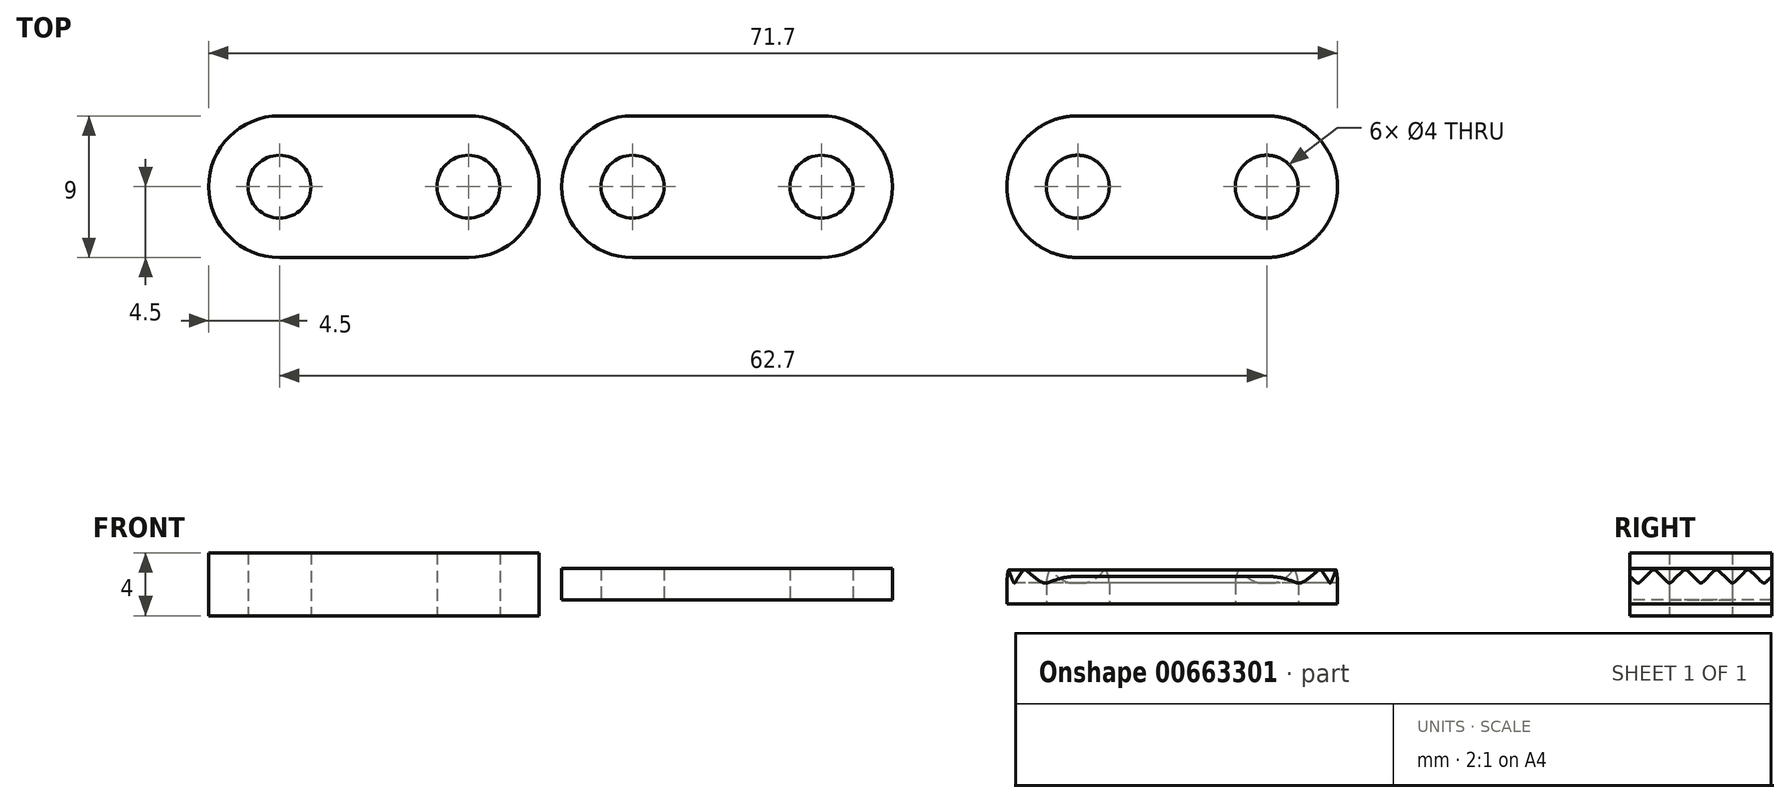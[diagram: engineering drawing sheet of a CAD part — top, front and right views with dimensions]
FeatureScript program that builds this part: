
annotation { "Feature Type Name" : "Feature", "Feature Type Description" : "" }
export const myFeature = defineFeature(function(context is Context, id is Id, definition is map)
    precondition{}
    {
        {
            var Q0;
            Q0=qCreatedBy(makeId("Top.planeOp"),FACE);
            var sketch = newSketch(context, id + "F0", { "sketchPlane" : qUnion([Q0])});
            skCircle(sketch, "E0", {"center": v(-56.7, 0) * mm, "radius": 4.5 * mm});
            skCircle(sketch, "E1", {"center": v(-44.7, 0) * mm, "radius": 4.5 * mm});
            skLineSegment(sketch, "E2", {"start": v(-44.7, 4.5) * mm, "end": v(-56.7, 4.5) * mm});
            skLineSegment(sketch, "E3", {"start": v(-56.7, -4.5) * mm, "end": v(-44.7, -4.5) * mm});
            skCircle(sketch, "E4", {"center": v(-56.7, 0) * mm, "radius": 2 * mm});
            skCircle(sketch, "E5", {"center": v(-44.7, 0) * mm, "radius": 2 * mm});
            skCircle(sketch, "E6", {"center": v(-34.28, 0) * mm, "radius": 4.5 * mm});
            skCircle(sketch, "E7", {"center": v(-22.28, 0) * mm, "radius": 4.5 * mm});
            skLineSegment(sketch, "E8", {"start": v(-22.28, 4.5) * mm, "end": v(-34.28, 4.5) * mm});
            skLineSegment(sketch, "E9", {"start": v(-34.28, -4.5) * mm, "end": v(-22.28, -4.5) * mm});
            skCircle(sketch, "E10", {"center": v(-34.28, 0) * mm, "radius": 2 * mm});
            skCircle(sketch, "E11", {"center": v(-22.28, 0) * mm, "radius": 2 * mm});
            skCircle(sketch, "E12", {"center": v(-6, 0) * mm, "radius": 4.5 * mm});
            skCircle(sketch, "E13", {"center": v(6, 0) * mm, "radius": 4.5 * mm});
            skLineSegment(sketch, "E14", {"start": v(6, 4.5) * mm, "end": v(-6, 4.5) * mm});
            skLineSegment(sketch, "E15", {"start": v(-6, -4.5) * mm, "end": v(6, -4.5) * mm});
            skCircle(sketch, "E16", {"center": v(-6, 0) * mm, "radius": 2 * mm});
            skCircle(sketch, "E17", {"center": v(6, 0) * mm, "radius": 2 * mm});
            skSolve(sketch);
        }
        {
            var Q0;
            Q0=makeQuery(id+"F0.imprint","IMPRINT",FACE,{"disambiguationData":[TD([[makeQuery(id+"F0.imprint","IMPRINT",EDGE,{"derivedFrom":sQuery(id+"F0.wireOp",EDGE,"E4")}),-1.0]])]});
            var Q1;
            Q1=makeQuery(id+"F0.imprint","IMPRINT",FACE,{"disambiguationData":[TD([[makeQuery(id+"F0.imprint","IMPRINT",EDGE,{"derivedFrom":sQuery(id+"F0.wireOp",EDGE,"E5")}),-1.0]])]});
            var Q2;
            {var subQ0=sQuery(id+"F0.wireOp",EDGE,"E2");Q2=makeQuery(id+"F0.imprint","IMPRINT",FACE,{"disambiguationData":[TD([[makeQuery(id+"F0.imprint","IMPRINT",EDGE,{"derivedFrom":subQ0}),1.0]])]});}
            extrude(context, id + "F1", {"entities" : qUnion([Q0, Q1, Q2]), "endBound" : BoundingType.SYMMETRIC, "depth" : 4 * mm, "offsetDistance" : 25 * mm});
        }
        {
            var Q0;
            Q0=makeQuery(id+"F0.imprint","IMPRINT",FACE,{"disambiguationData":[TD([[makeQuery(id+"F0.imprint","IMPRINT",EDGE,{"derivedFrom":sQuery(id+"F0.wireOp",EDGE,"E10")}),-1.0]])]});
            var Q1;
            {var subQ0=sQuery(id+"F0.wireOp",EDGE,"E8");Q1=makeQuery(id+"F0.imprint","IMPRINT",FACE,{"disambiguationData":[TD([[makeQuery(id+"F0.imprint","IMPRINT",EDGE,{"derivedFrom":subQ0}),1.0]])]});}
            var Q2;
            Q2=makeQuery(id+"F0.imprint","IMPRINT",FACE,{"disambiguationData":[TD([[makeQuery(id+"F0.imprint","IMPRINT",EDGE,{"derivedFrom":sQuery(id+"F0.wireOp",EDGE,"E11")}),-1.0]])]});
            extrude(context, id + "F2", {"entities" : qUnion([Q0, Q1, Q2]), "endBound" : BoundingType.SYMMETRIC, "depth" : 2 * mm, "offsetDistance" : 25 * mm});
        }
        {
            var Q0;
            Q0=makeQuery(id+"F0.imprint","IMPRINT",FACE,{"disambiguationData":[TD([[makeQuery(id+"F0.imprint","IMPRINT",EDGE,{"derivedFrom":sQuery(id+"F0.wireOp",EDGE,"E16")}),-1.0]])]});
            var Q1;
            {var subQ0=sQuery(id+"F0.wireOp",EDGE,"E14");Q1=makeQuery(id+"F0.imprint","IMPRINT",FACE,{"disambiguationData":[TD([[makeQuery(id+"F0.imprint","IMPRINT",EDGE,{"derivedFrom":subQ0}),1.0]])]});}
            var Q2;
            Q2=makeQuery(id+"F0.imprint","IMPRINT",FACE,{"disambiguationData":[TD([[makeQuery(id+"F0.imprint","IMPRINT",EDGE,{"derivedFrom":sQuery(id+"F0.wireOp",EDGE,"E17")}),-1.0]])]});
            extrude(context, id + "F3", {"entities" : qUnion([Q0, Q1, Q2]), "endBound" : BoundingType.SYMMETRIC, "depth" : 2.5 * mm, "offsetDistance" : 25 * mm});
        }
        {
            var Q0;
            Q0=qCreatedBy(makeId("Right.planeOp"),FACE);
            var sketch = newSketch(context, id + "F4", { "sketchPlane" : qUnion([Q0])});
            skLineSegment(sketch, "E18", {"start": v(-9.83, 0.17) * mm, "end": v(-9.14, 0.86) * mm});
            skLineSegment(sketch, "E19", {"start": v(-8.86, 0.86) * mm, "end": v(-8.14, 0.14) * mm});
            skLineSegment(sketch, "E20", {"start": v(-7.86, 0.14) * mm, "end": v(-7.14, 0.86) * mm});
            skLineSegment(sketch, "E21", {"start": v(-6.86, 0.86) * mm, "end": v(-6.14, 0.14) * mm});
            skPoint(sketch, "E22.visualSharp", {"position": v(-9, 1) * mm});
            skArc(sketch, "E22.filletArc", {"start": v(-8.86, 0.86) * mm, "mid": v(-9, 0.92) * mm, "end": v(-9.14, 0.86) * mm});
            skPoint(sketch, "E23.visualSharp", {"position": v(-7, 1) * mm});
            skArc(sketch, "E23.filletArc", {"start": v(-6.86, 0.86) * mm, "mid": v(-7, 0.92) * mm, "end": v(-7.14, 0.86) * mm});
            skPoint(sketch, "E24.visualSharp", {"position": v(-8, 0) * mm});
            skArc(sketch, "E24.filletArc", {"start": v(-8.14, 0.14) * mm, "mid": v(-8, 0.08) * mm, "end": v(-7.86, 0.14) * mm});
            skLineSegment(sketch, "E25", {"start": v(-5.86, 0.14) * mm, "end": v(-5.14, 0.86) * mm});
            skLineSegment(sketch, "E26", {"start": v(-4.86, 0.86) * mm, "end": v(-4.14, 0.14) * mm});
            skLineSegment(sketch, "E27", {"start": v(-3.86, 0.14) * mm, "end": v(-3.14, 0.86) * mm});
            skLineSegment(sketch, "E28", {"start": v(-2.86, 0.86) * mm, "end": v(-2.14, 0.14) * mm});
            skLineSegment(sketch, "E29", {"start": v(-1.86, 0.14) * mm, "end": v(-1.14, 0.86) * mm});
            skLineSegment(sketch, "E30", {"start": v(-0.86, 0.86) * mm, "end": v(-0.14, 0.14) * mm});
            skLineSegment(sketch, "E31", {"start": v(0.14, 0.14) * mm, "end": v(0.86, 0.86) * mm});
            skLineSegment(sketch, "E32", {"start": v(1.14, 0.86) * mm, "end": v(1.86, 0.14) * mm});
            skLineSegment(sketch, "E33", {"start": v(2.14, 0.14) * mm, "end": v(2.86, 0.86) * mm});
            skLineSegment(sketch, "E34", {"start": v(3.14, 0.86) * mm, "end": v(3.86, 0.14) * mm});
            skLineSegment(sketch, "E35", {"start": v(4.14, 0.14) * mm, "end": v(4.86, 0.86) * mm});
            skLineSegment(sketch, "E36", {"start": v(5.14, 0.86) * mm, "end": v(5.86, 0.14) * mm});
            skLineSegment(sketch, "E37", {"start": v(6.14, 0.14) * mm, "end": v(6.86, 0.86) * mm});
            skLineSegment(sketch, "E38", {"start": v(7.14, 0.86) * mm, "end": v(7.86, 0.14) * mm});
            skLineSegment(sketch, "E39", {"start": v(8.14, 0.14) * mm, "end": v(8.86, 0.86) * mm});
            skLineSegment(sketch, "E40", {"start": v(9.14, 0.86) * mm, "end": v(9.86, 0.14) * mm});
            skLineSegment(sketch, "E41", {"start": v(10.14, 0.14) * mm, "end": v(10.86, 0.86) * mm});
            skLineSegment(sketch, "E42", {"start": v(11.14, 0.86) * mm, "end": v(11.83, 0.17) * mm});
            skPoint(sketch, "E43.visualSharp", {"position": v(-5, 1) * mm});
            skArc(sketch, "E43.filletArc", {"start": v(-4.86, 0.86) * mm, "mid": v(-5, 0.92) * mm, "end": v(-5.14, 0.86) * mm});
            skPoint(sketch, "E44.visualSharp", {"position": v(-3, 1) * mm});
            skArc(sketch, "E44.filletArc", {"start": v(-2.86, 0.86) * mm, "mid": v(-3, 0.92) * mm, "end": v(-3.14, 0.86) * mm});
            skPoint(sketch, "E45.visualSharp", {"position": v(-1, 1) * mm});
            skArc(sketch, "E45.filletArc", {"start": v(-0.86, 0.86) * mm, "mid": v(-1, 0.92) * mm, "end": v(-1.14, 0.86) * mm});
            skPoint(sketch, "E46.visualSharp", {"position": v(1, 1) * mm});
            skArc(sketch, "E46.filletArc", {"start": v(1.14, 0.86) * mm, "mid": v(1, 0.92) * mm, "end": v(0.86, 0.86) * mm});
            skPoint(sketch, "E47.visualSharp", {"position": v(3, 1) * mm});
            skArc(sketch, "E47.filletArc", {"start": v(3.14, 0.86) * mm, "mid": v(3, 0.92) * mm, "end": v(2.86, 0.86) * mm});
            skPoint(sketch, "E48.visualSharp", {"position": v(5, 1) * mm});
            skArc(sketch, "E48.filletArc", {"start": v(5.14, 0.86) * mm, "mid": v(5, 0.92) * mm, "end": v(4.86, 0.86) * mm});
            skPoint(sketch, "E49.visualSharp", {"position": v(7, 1) * mm});
            skArc(sketch, "E49.filletArc", {"start": v(7.14, 0.86) * mm, "mid": v(7, 0.92) * mm, "end": v(6.86, 0.86) * mm});
            skPoint(sketch, "E50.visualSharp", {"position": v(9, 1) * mm});
            skArc(sketch, "E50.filletArc", {"start": v(9.14, 0.86) * mm, "mid": v(9, 0.92) * mm, "end": v(8.86, 0.86) * mm});
            skPoint(sketch, "E51.visualSharp", {"position": v(-6, 0) * mm});
            skArc(sketch, "E51.filletArc", {"start": v(-6.14, 0.14) * mm, "mid": v(-6, 0.08) * mm, "end": v(-5.86, 0.14) * mm});
            skPoint(sketch, "E52.visualSharp", {"position": v(-4, 0) * mm});
            skArc(sketch, "E52.filletArc", {"start": v(-4.14, 0.14) * mm, "mid": v(-4, 0.08) * mm, "end": v(-3.86, 0.14) * mm});
            skPoint(sketch, "E53.visualSharp", {"position": v(-2, 0) * mm});
            skArc(sketch, "E53.filletArc", {"start": v(-2.14, 0.14) * mm, "mid": v(-2, 0.08) * mm, "end": v(-1.86, 0.14) * mm});
            skPoint(sketch, "E54.visualSharp", {"position": v(0, 0) * mm});
            skArc(sketch, "E54.filletArc", {"start": v(-0.14, 0.14) * mm, "mid": v(0, 0.08) * mm, "end": v(0.14, 0.14) * mm});
            skPoint(sketch, "E55.visualSharp", {"position": v(2, 0) * mm});
            skArc(sketch, "E55.filletArc", {"start": v(1.86, 0.14) * mm, "mid": v(2, 0.08) * mm, "end": v(2.14, 0.14) * mm});
            skPoint(sketch, "E56.visualSharp", {"position": v(4, 0) * mm});
            skArc(sketch, "E56.filletArc", {"start": v(3.86, 0.14) * mm, "mid": v(4, 0.08) * mm, "end": v(4.14, 0.14) * mm});
            skPoint(sketch, "E57.visualSharp", {"position": v(6, 0) * mm});
            skArc(sketch, "E57.filletArc", {"start": v(5.86, 0.14) * mm, "mid": v(6, 0.08) * mm, "end": v(6.14, 0.14) * mm});
            skPoint(sketch, "E58.visualSharp", {"position": v(8, 0) * mm});
            skArc(sketch, "E58.filletArc", {"start": v(7.86, 0.14) * mm, "mid": v(8, 0.08) * mm, "end": v(8.14, 0.14) * mm});
            skPoint(sketch, "E59.visualSharp", {"position": v(10, 0) * mm});
            skArc(sketch, "E59.filletArc", {"start": v(9.86, 0.14) * mm, "mid": v(10, 0.08) * mm, "end": v(10.14, 0.14) * mm});
            skPoint(sketch, "E60.visualSharp", {"position": v(11, 1) * mm});
            skArc(sketch, "E60.filletArc", {"start": v(11.14, 0.86) * mm, "mid": v(11, 0.92) * mm, "end": v(10.86, 0.86) * mm});
            skLineSegment(sketch, "E61", {"start": v(-10, 1.86) * mm, "end": v(-10, 0.24) * mm});
            skLineSegment(sketch, "E62", {"start": v(-10, 1.86) * mm, "end": v(12, 1.86) * mm});
            skLineSegment(sketch, "E63", {"start": v(12, 0.24) * mm, "end": v(12, 1.86) * mm});
            skPoint(sketch, "E64.visualSharp", {"position": v(-10, 0) * mm});
            skArc(sketch, "E64.filletArc", {"start": v(-10, 0.24) * mm, "mid": v(-9.94, 0.15) * mm, "end": v(-9.83, 0.17) * mm});
            skPoint(sketch, "E65.visualSharp", {"position": v(12, 0) * mm});
            skArc(sketch, "E65.filletArc", {"start": v(11.83, 0.17) * mm, "mid": v(11.94, 0.15) * mm, "end": v(12, 0.24) * mm});
            skSolve(sketch);
        }
        {
            var Q0;
            Q0=makeQuery(id+"F4.imprint","IMPRINT",FACE,{"disambiguationData":[TD([[makeQuery(id+"F4.imprint","IMPRINT",EDGE,{"derivedFrom":sQuery(id+"F4.wireOp",EDGE,"E18")}),1.0]])]});
            extrude(context, id + "F5", {"entities" : qUnion([Q0]), "operationType" : NewBodyOperationType.REMOVE, "endBound" : BoundingType.SYMMETRIC, "depth" : 25 * mm, "offsetDistance" : 25 * mm});
        }
    });
